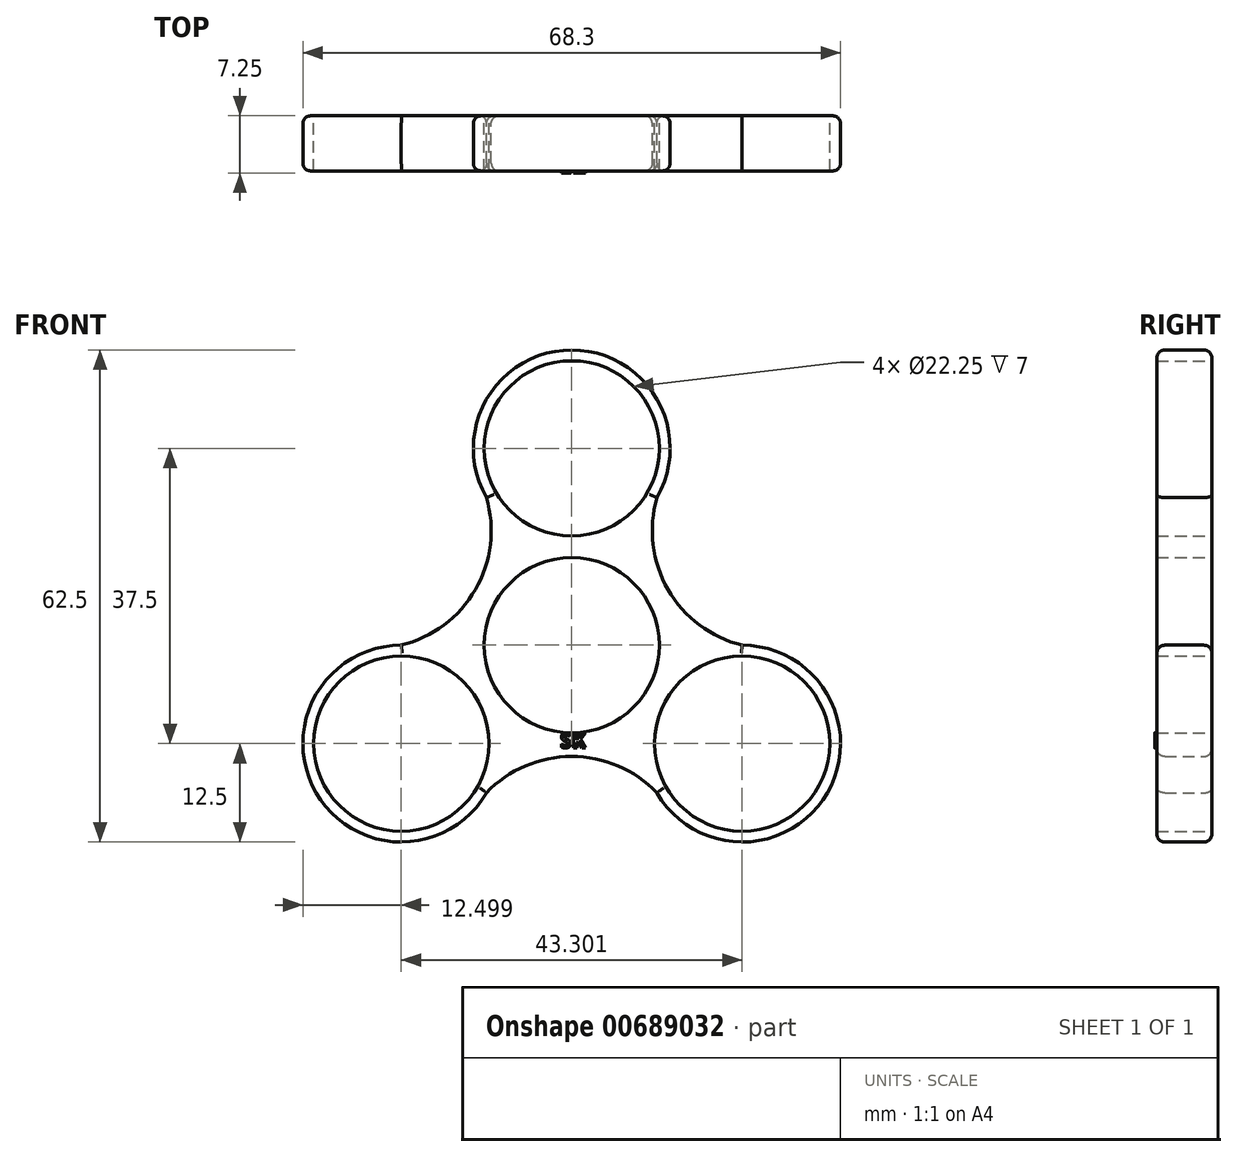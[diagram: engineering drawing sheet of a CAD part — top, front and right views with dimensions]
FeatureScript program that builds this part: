
annotation { "Feature Type Name" : "Feature", "Feature Type Description" : "" }
export const myFeature = defineFeature(function(context is Context, id is Id, definition is map)
    precondition{}
    {
        {
            var Q0;
            Q0=qCreatedBy(makeId("Front.planeOp"),FACE);
            var sketch = newSketch(context, id + "F0", { "sketchPlane" : qUnion([Q0])});
            skCircle(sketch, "E0", {"center": v(0, 0) * mm, "radius": 11.12 * mm});
            skCircle(sketch, "E1", {"center": v(0, 25) * mm, "radius": 11.12 * mm});
            skCircle(sketch, "E2", {"center": v(21.65, -12.5) * mm, "radius": 11.12 * mm});
            skCircle(sketch, "E3", {"center": v(-21.65, -12.5) * mm, "radius": 11.12 * mm});
            skArc(sketch, "E4", {"start": v(10.83, 18.75) * mm, "mid": v(0, 37.5) * mm, "end": v(-10.83, 18.75) * mm});
            skArc(sketch, "E5", {"start": v(10.83, -18.75) * mm, "mid": v(32.48, -18.75) * mm, "end": v(21.65, 0) * mm});
            skArc(sketch, "E6", {"start": v(-21.65, 0) * mm, "mid": v(-32.48, -18.75) * mm, "end": v(-10.83, -18.75) * mm});
            skArc(sketch, "E7", {"start": v(-21.65, 0) * mm, "mid": v(-12.24, 7.07) * mm, "end": v(-10.83, 18.75) * mm});
            skArc(sketch, "E8", {"start": v(10.83, 18.75) * mm, "mid": v(12.24, 7.07) * mm, "end": v(21.65, 0) * mm});
            skArc(sketch, "E9", {"start": v(10.83, -18.75) * mm, "mid": v(0, -14.13) * mm, "end": v(-10.83, -18.75) * mm});
            skSolve(sketch);
        }
        {
            var Q0;
            Q0=makeQuery(id+"F0.imprint","IMPRINT",FACE,{"disambiguationData":[TD([[makeQuery(id+"F0.imprint","IMPRINT",EDGE,{"derivedFrom":sQuery(id+"F0.wireOp",EDGE,"E0")}),-1.0]])]});
            extrude(context, id + "F1", {"entities" : qUnion([Q0]), "depth" : 7 * mm, "offsetDistance" : 25 * mm});
        }
        {
            var Q0;
            Q0=makeQuery(id+"F1.opExtrude","CAP_EDGE",EDGE,{"disambiguationData":[OSD([sQuery(id+"F0.wireOp",EDGE,"E4")])],"isStart":false});
            var Q1;
            Q1=makeQuery(id+"F1.opExtrude","CAP_EDGE",EDGE,{"disambiguationData":[OSD([sQuery(id+"F0.wireOp",EDGE,"E8")])],"isStart":false});
            var Q2;
            Q2=makeQuery(id+"F1.opExtrude","CAP_EDGE",EDGE,{"disambiguationData":[OSD([sQuery(id+"F0.wireOp",EDGE,"E5")])],"isStart":false});
            var Q3;
            Q3=makeQuery(id+"F1.opExtrude","CAP_EDGE",EDGE,{"disambiguationData":[OSD([sQuery(id+"F0.wireOp",EDGE,"E9")])],"isStart":false});
            var Q4;
            Q4=makeQuery(id+"F1.opExtrude","CAP_EDGE",EDGE,{"disambiguationData":[OSD([sQuery(id+"F0.wireOp",EDGE,"E6")])],"isStart":false});
            var Q5;
            Q5=makeQuery(id+"F1.opExtrude","CAP_EDGE",EDGE,{"disambiguationData":[OSD([sQuery(id+"F0.wireOp",EDGE,"E7")])],"isStart":false});
            fillet(context, id + "F2", {"entities" : qUnion([Q0, Q1, Q2, Q3, Q4, Q5]), "radius" : 1 * mm, "tangentPropagation" : true, "allowEdgeOverflow" : false});
        }
        {
            var Q0;
            Q0=makeQuery(id+"F1.opExtrude","CAP_EDGE",EDGE,{"disambiguationData":[OSD([sQuery(id+"F0.wireOp",EDGE,"E6")])],"isStart":true});
            var Q1;
            Q1=makeQuery(id+"F1.opExtrude","CAP_EDGE",EDGE,{"disambiguationData":[OSD([sQuery(id+"F0.wireOp",EDGE,"E9")])],"isStart":true});
            var Q2;
            Q2=makeQuery(id+"F1.opExtrude","CAP_EDGE",EDGE,{"disambiguationData":[OSD([sQuery(id+"F0.wireOp",EDGE,"E5")])],"isStart":true});
            var Q3;
            Q3=makeQuery(id+"F1.opExtrude","CAP_EDGE",EDGE,{"disambiguationData":[OSD([sQuery(id+"F0.wireOp",EDGE,"E8")])],"isStart":true});
            var Q4;
            Q4=makeQuery(id+"F1.opExtrude","CAP_EDGE",EDGE,{"disambiguationData":[OSD([sQuery(id+"F0.wireOp",EDGE,"E4")])],"isStart":true});
            var Q5;
            Q5=makeQuery(id+"F1.opExtrude","CAP_EDGE",EDGE,{"disambiguationData":[OSD([sQuery(id+"F0.wireOp",EDGE,"E7")])],"isStart":true});
            fillet(context, id + "F3", {"entities" : qUnion([Q0, Q1, Q2, Q3, Q4, Q5]), "radius" : 1 * mm, "tangentPropagation" : true, "allowEdgeOverflow" : false});
        }
        {
            var Q0;
            Q0=makeQuery(id+"F1.opExtrude","CAP_FACE",FACE,{"disambiguationData":[OSD([sQuery(id+"F0.wireOp",EDGE,"E0"),sQuery(id+"F0.wireOp",EDGE,"E1"),sQuery(id+"F0.wireOp",EDGE,"E2"),sQuery(id+"F0.wireOp",EDGE,"E3"),sQuery(id+"F0.wireOp",EDGE,"E4"),sQuery(id+"F0.wireOp",EDGE,"E5"),sQuery(id+"F0.wireOp",EDGE,"E6"),sQuery(id+"F0.wireOp",EDGE,"E7"),sQuery(id+"F0.wireOp",EDGE,"E8"),sQuery(id+"F0.wireOp",EDGE,"E9")])],"isStart":false});
            var sketch = newSketch(context, id + "F4", { "sketchPlane" : qUnion([Q0])});
            skText(sketch, "E10", { "text": "SK", "fontName": "OpenSans-Bold.ttf"});
            const initialGuessF4  = {"E10": [-0.00145, -0.01303, 1, 0, 0.0019]};
            skSetInitialGuess(sketch, initialGuessF4);
            skSolve(sketch);
        }
        {
            var Q0;
            Q0 = qSketchRegion(id + "F4", true);
            extrude(context, id + "F5", {"entities" : qUnion([Q0]), "operationType" : NewBodyOperationType.ADD, "depth" : .25 * mm, "offsetDistance" : 25 * mm});
        }
    });
